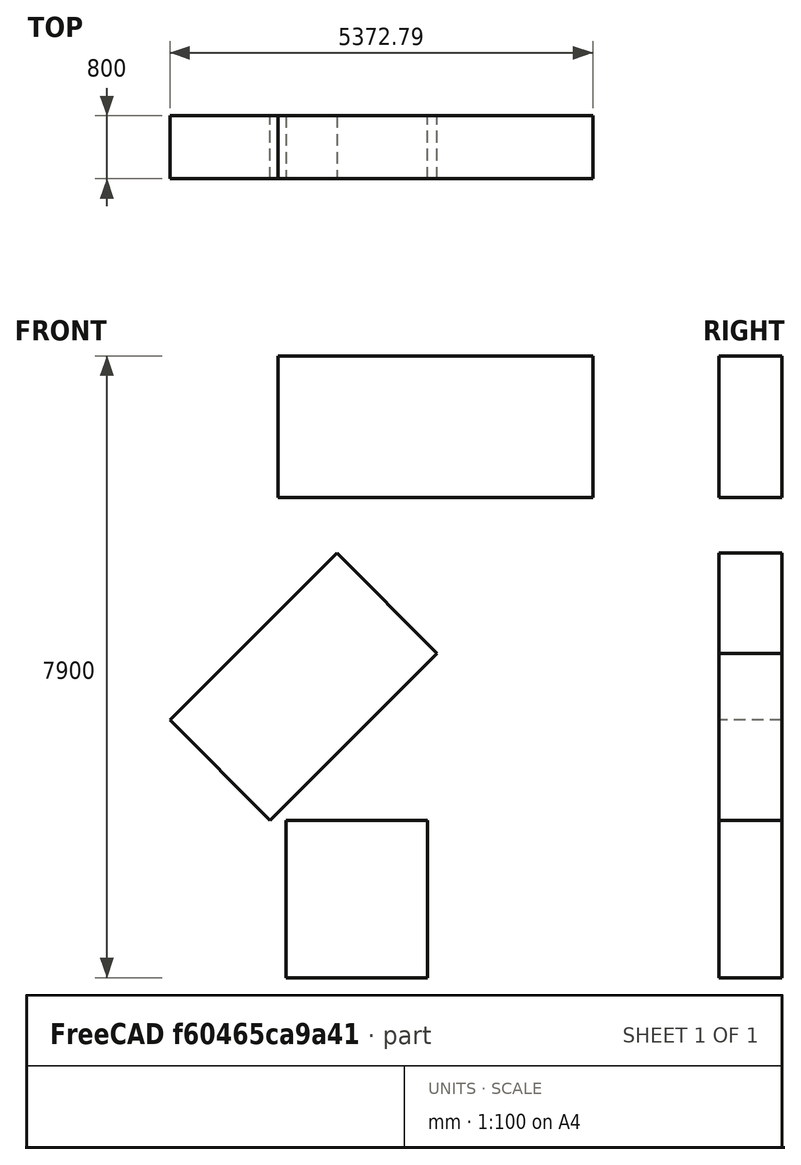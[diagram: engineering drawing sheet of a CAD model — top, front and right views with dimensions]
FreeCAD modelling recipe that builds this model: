
FCSTD DOCUMENT  (FreeCAD 0.19R21059 (Git))
Label: multiple extrusions
License: All rights reserved
LicenseURL: http://en.wikipedia.org/wiki/All_rights_reserved
objects: Part::Part2DObjectPython×3, Part::Extrusion×3
note: 6 computed .brp shape members not serialized (recipe doc carries the construction recipe); baked Part::Feature solids carry a one-line shape summary decoded from their .brp

FEATURE [Part::Part2DObjectPython] Rectangle  # Draft 2D object (typed FeaturePython)
  Area = 1.44e+06
  ChamferSize = 0
  Columns = 1
  FilletRadius = 0
  Height = 800
  Length = 1800
  MakeFace = true
  Placement = pos=(100,-900,0) rot=(0,0,1;0rad)
  Rows = 1
FEATURE [Part::Extrusion] Extrude
  Base = -> Rectangle
  Dir = (0,0,1)
  DirMode = 2
  FaceMakerClass = Part::FaceMakerBullseye
  LengthFwd = 2000
  LengthRev = 0
  Solid = false
  Symmetric = false
FEATURE [Part::Part2DObjectPython] Rectangle001  # Draft 2D object (typed FeaturePython)
  Area = 1.44e+06
  ChamferSize = 0
  Columns = 1
  FilletRadius = 0
  Height = 800
  Length = 1800
  MakeFace = true
  Placement = pos=(-1372.79,-900,3272.79) rot=(0,1,0;0.785398rad)
  Rows = 1
FEATURE [Part::Extrusion] Extrude001
  Base = -> Rectangle001
  Dir = (0.707107,0,0.707107)
  DirMode = 2
  FaceMakerClass = Part::FaceMakerBullseye
  LengthFwd = 3000
  LengthRev = 0
  Solid = false
  Symmetric = false
FEATURE [Part::Part2DObjectPython] Rectangle002  # Draft 2D object (typed FeaturePython)
  Area = 1.44e+06
  ChamferSize = 0
  Columns = 1
  FilletRadius = 0
  Height = 800
  Length = 1800
  MakeFace = true
  Placement = pos=(0,-900,7900) rot=(0,1,0;1.5708rad)
  Rows = 1
FEATURE [Part::Extrusion] Extrude002
  Base = -> Rectangle002
  Dir = (1,0,-2e-16)
  DirMode = 2
  FaceMakerClass = Part::FaceMakerBullseye
  LengthFwd = 4000
  LengthRev = 0
  Solid = false
  Symmetric = false
